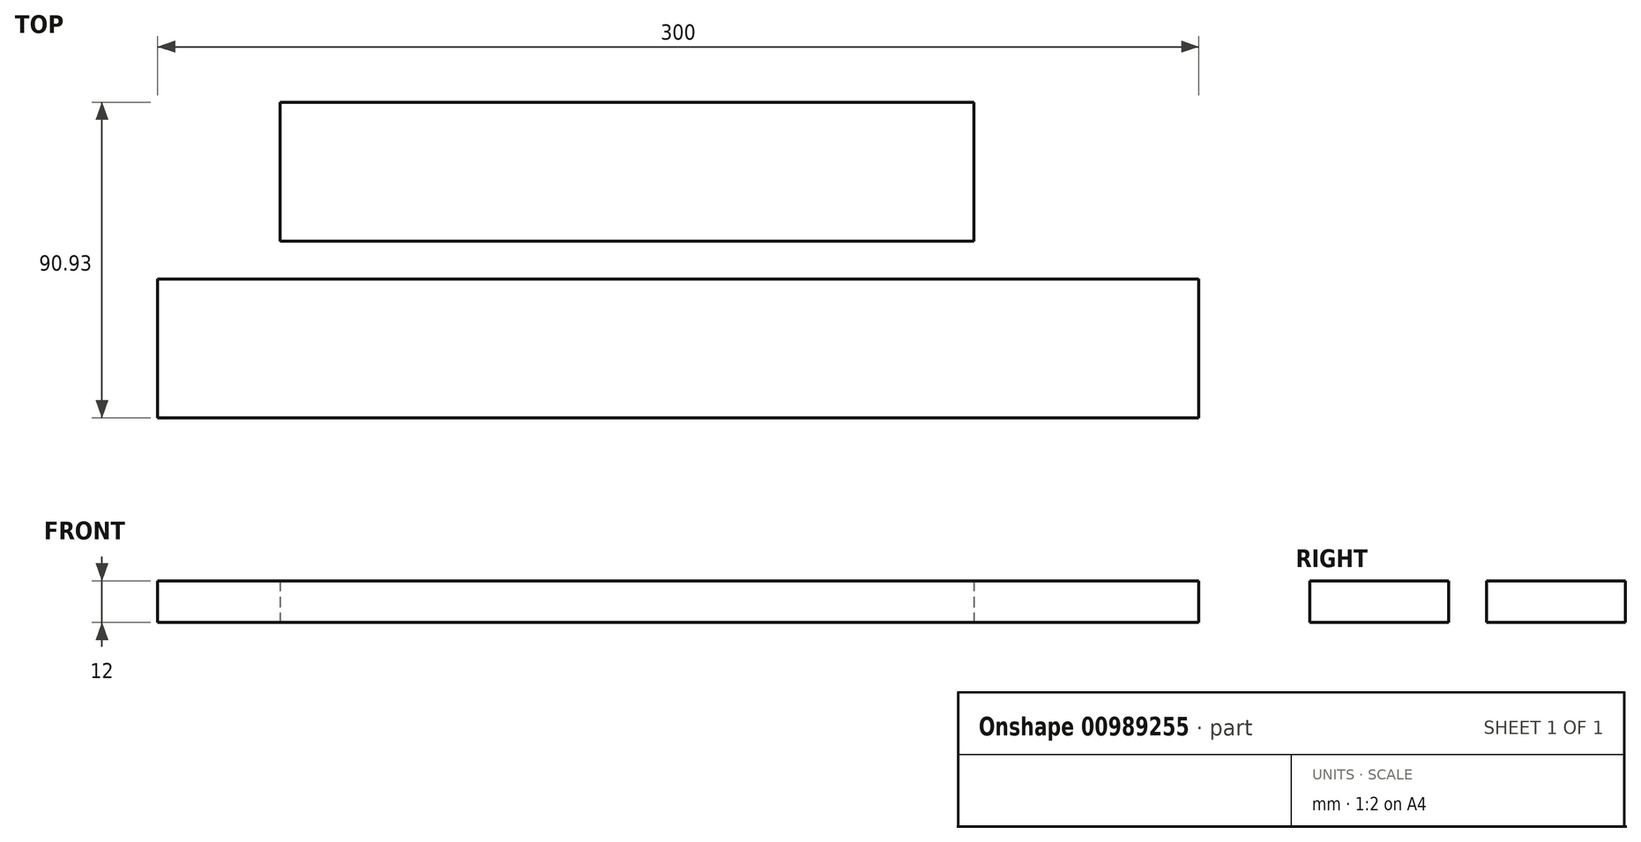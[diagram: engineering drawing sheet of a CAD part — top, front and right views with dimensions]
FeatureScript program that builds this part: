
annotation { "Feature Type Name" : "Feature", "Feature Type Description" : "" }
export const myFeature = defineFeature(function(context is Context, id is Id, definition is map)
    precondition{}
    {
        {
            var Q0;
            Q0=qCreatedBy(makeId("Top.planeOp"),FACE);
            var sketch = newSketch(context, id + "F0", { "sketchPlane" : qUnion([Q0])});
            skLineSegment(sketch, "E0.bottom", {"start": v(-150, 20) * mm, "end": v(150, 20) * mm});
            skLineSegment(sketch, "E0.top", {"start": v(-150, -20) * mm, "end": v(150, -20) * mm});
            skLineSegment(sketch, "E0.left", {"start": v(-150, 20) * mm, "end": v(-150, -20) * mm});
            skLineSegment(sketch, "E0.right", {"start": v(150, 20) * mm, "end": v(150, -20) * mm});
            skPoint(sketch, "E0.middle", {"position": v(0, 0) * mm});
            skSolve(sketch);
        }
        {
            var Q0;
            Q0 = qSketchRegion(id + "F0", true);
            extrude(context, id + "F1", {"entities" : qUnion([Q0]), "depth" : 12 * mm, "offsetDistance" : 25 * mm});
        }
        {
            var Q0;
            Q0=qCreatedBy(makeId("Top.planeOp"),FACE);
            var sketch = newSketch(context, id + "F2", { "sketchPlane" : qUnion([Q0])});
            skLineSegment(sketch, "E1.bottom", {"start": v(-114.76, 70.93) * mm, "end": v(85.24, 70.93) * mm});
            skLineSegment(sketch, "E1.top", {"start": v(-114.76, 30.93) * mm, "end": v(85.24, 30.93) * mm});
            skLineSegment(sketch, "E1.left", {"start": v(-114.76, 70.93) * mm, "end": v(-114.76, 30.93) * mm});
            skLineSegment(sketch, "E1.right", {"start": v(85.24, 70.93) * mm, "end": v(85.24, 30.93) * mm});
            skSolve(sketch);
        }
        {
            var Q0;
            Q0 = qSketchRegion(id + "F2", true);
            extrude(context, id + "F3", {"entities" : qUnion([Q0]), "depth" : 12 * mm, "offsetDistance" : 25 * mm});
        }
    });
